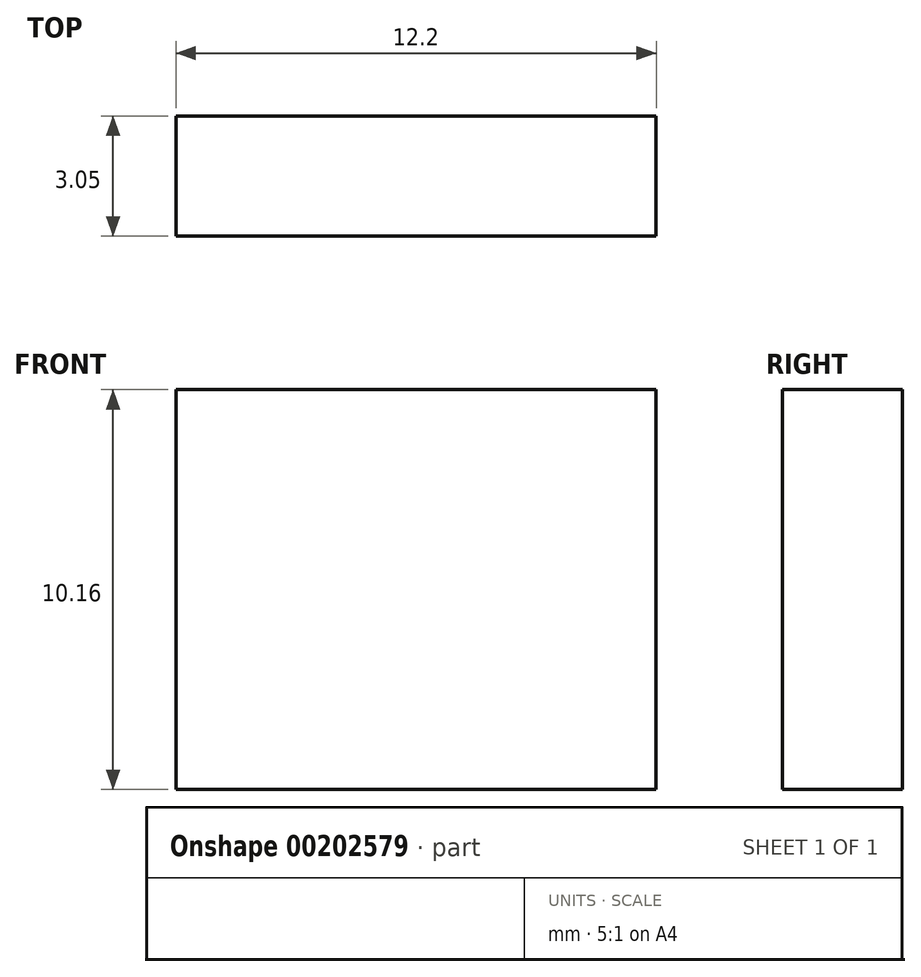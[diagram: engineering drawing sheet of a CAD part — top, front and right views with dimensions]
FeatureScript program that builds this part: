
annotation { "Feature Type Name" : "Feature", "Feature Type Description" : "" }
export const myFeature = defineFeature(function(context is Context, id is Id, definition is map)
    precondition{}
    {
        {
            var Q0;
            Q0=qCreatedBy(makeId("Front.planeOp"),FACE);
            var sketch = newSketch(context, id + "F0", { "sketchPlane" : qUnion([Q0])});
            skLineSegment(sketch, "E0.bottom", {"start": v(-6.1, 5.08) * mm, "end": v(6.1, 5.08) * mm});
            skLineSegment(sketch, "E0.top", {"start": v(-6.1, -5.08) * mm, "end": v(6.1, -5.08) * mm});
            skLineSegment(sketch, "E0.left", {"start": v(-6.1, 5.08) * mm, "end": v(-6.1, -5.08) * mm});
            skLineSegment(sketch, "E0.right", {"start": v(6.1, 5.08) * mm, "end": v(6.1, -5.08) * mm});
            skSolve(sketch);
        }
        {
            var Q0;
            Q0=makeQuery(id+"F0.imprint","IMPRINT",FACE,{"disambiguationData":[TD([[makeQuery(id+"F0.imprint","IMPRINT",EDGE,{"derivedFrom":sQuery(id+"F0.wireOp",EDGE,"E0.bottom")}),-1.0]])]});
            extrude(context, id + "F1", {"entities" : qUnion([Q0]), "depth" : 3.05 * mm});
        }
    });
